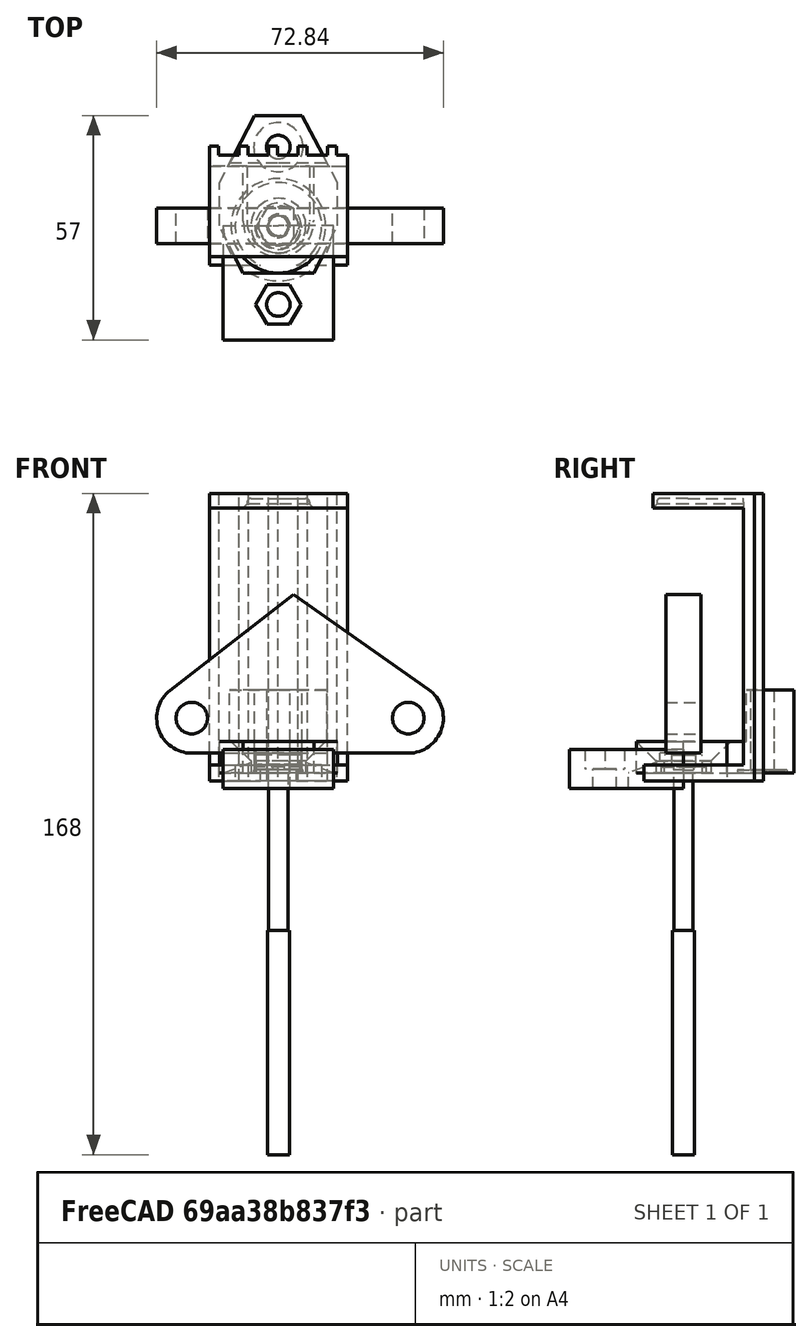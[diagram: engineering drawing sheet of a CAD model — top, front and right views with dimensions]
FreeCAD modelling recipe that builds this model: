
FCSTD DOCUMENT  (FreeCAD 1.0R1.0.1)
Label: stopper
License: All rights reserved
LicenseURL: http://en.wikipedia.org/wiki/All_rights_reserved
objects: Sketcher::SketchObject×19, PartDesign::Pad×12, App::Link×8, App::FeaturePython×8, PartDesign::Body×6, PartDesign::Pocket×4, PartDesign::Chamfer×3, Assembly::JointGroup×2, Assembly::AssemblyObject×2, Part::Revolution×1, Part::Extrusion×1, Image::ImagePlane×1, PartDesign::LinearPattern×1, PartDesign::Fillet×1, PartDesign::FeatureBase×1, Assembly::AssemblyLink×1, PartDesign::Revolution×1
note: 113 computed .brp shape members not serialized (recipe doc carries the construction recipe); baked Part::Feature solids carry a one-line shape summary decoded from their .brp

FEATURE [Sketcher::SketchObject] Sketch  label="Cyl"
  ArcFitTolerance = 1e-06
  FullyConstrained = true
  MakeInternals = false
  Placement = pos=(0,0,0) rot=(1,0,0;1.5708rad)
  sketch-geometry (15):
    g0: LineSegment StartX=0 StartY=0 StartZ=0 EndX=8 EndY=0 EndZ=0
    g1: LineSegment StartX=8 StartY=0 StartZ=0 EndX=14 EndY=6 EndZ=0
    g2: LineSegment StartX=14 StartY=6 StartZ=0 EndX=14 EndY=36.824 EndZ=0
    g3: LineSegment StartX=14 StartY=36.824 StartZ=0 EndX=15.2 EndY=36.824 EndZ=0
    g4: LineSegment StartX=15.2 StartY=36.824 StartZ=0 EndX=14.8 EndY=37.9406 EndZ=0
    g5: LineSegment StartX=14.8 StartY=37.9406 StartZ=0 EndX=14.8 EndY=53 EndZ=0
    g6: LineSegment StartX=14.8 StartY=53 StartZ=0 EndX=12.5 EndY=56 EndZ=0
    g7: LineSegment StartX=12.5 StartY=56 StartZ=0 EndX=12.5 EndY=62.6 EndZ=0
    g8: LineSegment StartX=12.5 StartY=62.6 StartZ=0 EndX=6 EndY=65.6 EndZ=0
    g9: LineSegment StartX=6 StartY=65.6 StartZ=0 EndX=6 EndY=67.6 EndZ=0
    g10: LineSegment StartX=6 StartY=67.6 StartZ=0 EndX=0 EndY=67.6 EndZ=0
    g11: LineSegment StartX=0 StartY=-0.8 StartZ=0 EndX=6.56 EndY=-0.8 EndZ=0
    g12: LineSegment StartX=6.56 StartY=-0.8 StartZ=0 EndX=6.56 EndY=0 EndZ=0
    g13: LineSegment StartX=0 StartY=-4.1 StartZ=0 EndX=4 EndY=-4.1 EndZ=0
    g14: LineSegment StartX=4 StartY=-4.1 StartZ=0 EndX=4 EndY=-0.8 EndZ=0
  constraints (46):
    c: Coincident(g-1,g0)
    c: PointOnObject(g0,g-1)
    c: Coincident(g0,g1)
    c: Coincident(g1,g2)
    c: Vertical(g2)
    c: Coincident(g2,g3)
    c: Coincident(g3,g4)
    c: Coincident(g4,g5)
    c: Vertical(g5)
    c: Coincident(g5,g6)
    c: Angle(g1,g-1) = 2.35619
    c: DistanceX(g0,g0) = 8
    c: Distance(g2,g-2) = 14
    c: Distance(g3,g-2) = 15.2
    c: Horizontal(g3)
    c: Distance(g5,g-2) = 14.8
    c: Block(g4)
    c: Distance(g6,g-1) = 56
    c: Coincident(g6,g7)
    c: Vertical(g7)
    c: Coincident(g7,g8)
    c: DistanceY(g7,g7) = 6.6
    c: Distance(g7,g-2) = 12.5
    c: DistanceY(g6,g6) = 3
    c: DistanceY(g7,g8) = 3
    c: Distance(g8,g-2) = 6
    c: Coincident(g8,g9)
    c: Vertical(g9)
    c: Coincident(g9,g10)
    c: PointOnObject(g10,g-2)
    c: Horizontal(g10)
    c: DistanceY(g9,g9) = 2
    c: PointOnObject(g11,g-2)
    c: Horizontal(g11)
    c: Coincident(g11,g12)
    c: PointOnObject(g12,g0)
    c: Vertical(g12)
    c: DistanceX(g11,g11) = 6.56
    c: DistanceY(g12,g12) = 0.8
    c: PointOnObject(g13,g-2)
    c: Horizontal(g13)
    c: Coincident(g13,g14)
    c: PointOnObject(g14,g11)
    c: Vertical(g14)
    c: DistanceX(g13,g13) = 4
    c: DistanceY(g14,g14) = 3.3
FEATURE [Sketcher::SketchObject] Sketch001  label="boss-s"
  ArcFitTolerance = 1e-06
  FullyConstrained = false
  MakeInternals = false
  Placement = pos=(0,0,0) rot=(1,0,0;1.5708rad)
  sketch-geometry (8):
    g0: LineSegment StartX=0 StartY=5 StartZ=0 EndX=33 EndY=5 EndZ=0
    g1: ArcOfCircle CenterX=33 CenterY=13.9161 CenterZ=0 NormalX=0 NormalY=0 NormalZ=1 AngleXU=0 Radius=8.91608 StartAngle=4.71239 EndAngle=7.24
    g2: LineSegment StartX=38.1368 StartY=21.2037 StartZ=0 EndX=3.88315 EndY=45.3479 EndZ=0
    g3: LineSegment StartX=3.88315 StartY=45.3479 StartZ=0 EndX=-27.4747 EndY=20.9535 EndZ=0
    g4: ArcOfCircle CenterX=-22 CenterY=13.9161 CenterZ=0 NormalX=0 NormalY=0 NormalZ=1 AngleXU=0 Radius=8.91608 StartAngle=2.23194 EndAngle=4.71239
    g5: LineSegment StartX=-22 StartY=5 StartZ=0 EndX=0 EndY=5 EndZ=0
    g6: Circle CenterX=-22 CenterY=13.9161 CenterZ=0 NormalX=0 NormalY=0 NormalZ=1 AngleXU=0 Radius=4
    g7: Circle CenterX=33 CenterY=13.9161 CenterZ=0 NormalX=0 NormalY=0 NormalZ=1 AngleXU=0 Radius=4
  constraints (17):
    c: PointOnObject(g0,g-2)
    c: Horizontal(g0)
    c: Tangent(g0,g1) = -1.5708
    c: Tangent(g1,g2) = -1.5708
    c: Coincident(g2,g3)
    c: Tangent(g3,g4) = -1.5708
    c: Tangent(g4,g5) = -1.5708
    c: Coincident(g5,g0)
    c: Horizontal(g4,g1)
    c: Distance(g1,g-2) = 33
    c: Distance(g4,g-2) = 22
    c: Parallel(g5,g0)
    c: Distance(g-1,g0) = 5
    c: Coincident(g6,g4)
    c: Diameter(g6) = 8
    c: Coincident(g7,g1)
    c: Diameter(g7) = 8
FEATURE [Part::Revolution] Revolve  label="cylinterd"
  Angle = 360
  Axis = (0,0,1)
  Base = (0,0,0)
  FaceMakerClass = Part::FaceMakerBullseye
  Solid = false
  Source = -> Sketch
  Symmetric = false
FEATURE [Part::Extrusion] Extrude  label="boss"
  Base = -> Sketch001
  Dir = (0,-1,2e-16)
  DirMode = 2
  FaceMakerClass = Part::FaceMakerBullseye
  FaceMakerMode = 3
  LengthFwd = 9
  LengthRev = 0
  Solid = true
  Symmetric = true
FEATURE [Image::ImagePlane] oemtension
  Placement = pos=(5.44,31.83,30.09) rot=(0.839369,-0.207279,0.502488;2.2068rad)
  XSize = 98.798
  YSize = 74.102
FEATURE [Sketcher::SketchObject] Sketch004  label="retainR-s"
  ArcFitTolerance = 1e-06
  AttachmentSupport = -> [XY_Plane]
  FullyConstrained = true
  MakeInternals = false
  MapMode = 5
  sketch-geometry (7):
    g0: LineSegment StartX=17.5 StartY=-10 StartZ=0 EndX=17.5 EndY=18 EndZ=0
    g1: LineSegment StartX=17.5 StartY=18 StartZ=0 EndX=-17.5 EndY=18 EndZ=0
    g2: LineSegment StartX=-17.5 StartY=18 StartZ=0 EndX=-17.5 EndY=-10 EndZ=0
    g3: LineSegment StartX=-17.5 StartY=-10 StartZ=0 EndX=-4.58258 EndY=-10 EndZ=0
    g4: GeomPoint X=0 Y=18 Z=0
    g5: ArcOfCircle CenterX=0 CenterY=0 CenterZ=0 NormalX=0 NormalY=0 NormalZ=1 AngleXU=0 Radius=11 StartAngle=5.14209 EndAngle=10.5659
    g6: LineSegment StartX=4.58258 StartY=-10 StartZ=0 EndX=17.5 EndY=-10 EndZ=0
  constraints (20):
    c: Coincident(g0,g1)
    c: Coincident(g1,g2)
    c: Coincident(g2,g3)
    c: Coincident(g6,g0)
    c: Vertical(g0)
    c: Vertical(g2)
    c: Horizontal(g1)
    c: Horizontal(g3)
    c: Distance(g1,g1) = 35
    c: DistanceY(g0,g0) = 28
    c: PointOnObject(g4,g-2)
    c: Distance(g1,g-1) = 18
    c: Symmetric(g1,g0,g4)
    c: Coincident(g5,g-1)
    c: Diameter(g5) = 22
    c: PointOnObject(g5,g6)
    c: Coincident(g3,g5)
    c: PointOnObject(g6,g5)
    c: Horizontal(g6)
    c: Distance(g1,g3) = 28
FEATURE [PartDesign::Pad] Pad  label="ring"
  Direction = (0,0,1)
  Length = 4
  Length2 = 10
  Midplane = true
  Profile = -> Sketch004
  ReferenceAxis = -> Sketch004 [N_Axis]
  Suppressed = false
  Type = 0
FEATURE [Sketcher::SketchObject] Sketch005  label="reatinback-s"
  ArcFitTolerance = 1e-06
  AttachmentSupport = -> [Pad]
  ExternalGeometry = -> [Pad]
  FullyConstrained = true
  MakeInternals = false
  MapMode = 5
  Placement = pos=(0,0,2) rot=(0,0,1;0rad)
  sketch-geometry (4):
    g0: LineSegment StartX=17.5 StartY=18 StartZ=0 EndX=-17.5 EndY=18 EndZ=0
    g1: LineSegment StartX=-17.5 StartY=18 StartZ=0 EndX=-17.5 EndY=15.2 EndZ=0
    g2: LineSegment StartX=-17.5 StartY=15.2 StartZ=0 EndX=17.5 EndY=15.2 EndZ=0
    g3: LineSegment StartX=17.5 StartY=15.2 StartZ=0 EndX=17.5 EndY=18 EndZ=0
  constraints (10):
    c: Coincident(g0,g1)
    c: Coincident(g1,g2)
    c: Coincident(g2,g3)
    c: Coincident(g3,g0)
    c: Horizontal(g2)
    c: Vertical(g1)
    c: Vertical(g3)
    c: Coincident(g-3,g0)
    c: Coincident(g0,g-3)
    c: DistanceY(g3,g3) = 2.8
FEATURE [PartDesign::Pad] Pad001  label="spine"
  BaseFeature = -> Pad
  Direction = (0,0,1)
  Length = 69
  Length2 = 10
  Profile = -> Sketch005
  ReferenceAxis = -> Sketch005 [N_Axis]
  Suppressed = false
  Type = 0
FEATURE [Sketcher::SketchObject] Sketch006
  ArcFitTolerance = 1e-06
  AttachmentSupport = -> [Pad001]
  ExternalGeometry = -> [Pad001]
  FullyConstrained = true
  MakeInternals = false
  MapMode = 5
  Placement = pos=(0,15.2,0) rot=(1,0,0;1.5708rad)
  sketch-geometry (5):
    g0: LineSegment StartX=-17.5 StartY=71 StartZ=0 EndX=-17.5 EndY=69.75 EndZ=0
    g1: LineSegment StartX=-17.5 StartY=69.75 StartZ=0 EndX=17.5 EndY=69.75 EndZ=0
    g2: LineSegment StartX=17.5 StartY=69.75 StartZ=0 EndX=17.5 EndY=71 EndZ=0
    g3: LineSegment StartX=17.5 StartY=71 StartZ=0 EndX=-17.5 EndY=71 EndZ=0
    g4: GeomPoint X=3.6e-15 Y=71 Z=0
  constraints (11):
    c: Coincident(g0,g1)
    c: Coincident(g1,g2)
    c: Coincident(g2,g3)
    c: Coincident(g3,g0)
    c: Vertical(g0)
    c: Vertical(g2)
    c: Horizontal(g1)
    c: Symmetric(g-3,g-3,g4)
    c: Coincident(g2,g-3)
    c: Coincident(g0,g-3)
    c: DistanceY(g0,g0) = 1.25
FEATURE [PartDesign::Pad] Pad002  label="fngr"
  BaseFeature = -> Pad001
  Direction = (0,-1,2e-16)
  Length = 23
  Length2 = 10
  Profile = -> Sketch006
  ReferenceAxis = -> Sketch006 [N_Axis]
  Suppressed = false
  Type = 0
FEATURE [Sketcher::SketchObject] Sketch007
  ArcFitTolerance = 1e-06
  AttachmentSupport = -> [Pad001]
  ExternalGeometry = -> [Pad001]
  FullyConstrained = true
  MakeInternals = false
  MapMode = 5
  Placement = pos=(0,18,0) rot=(0,0.707107,0.707107;3.14159rad)
  sketch-geometry (5):
    g0: LineSegment StartX=17.5 StartY=-2 StartZ=0 EndX=17.5 EndY=71 EndZ=0
    g1: LineSegment StartX=17.5 StartY=71 StartZ=0 EndX=15.2 EndY=71 EndZ=0
    g2: LineSegment StartX=15.2 StartY=71 StartZ=0 EndX=15.2 EndY=-2 EndZ=0
    g3: LineSegment StartX=15.2 StartY=-2 StartZ=0 EndX=17.5 EndY=-2 EndZ=0
    g4: GeomPoint X=16.35 Y=34.5 Z=0
  constraints (10):
    c: Coincident(g0,g1)
    c: Coincident(g1,g2)
    c: Coincident(g2,g3)
    c: Coincident(g3,g0)
    c: Horizontal(g1)
    c: Symmetric(g1,g0,g4)
    c: Symmetric(g2,g0,g4)
    c: DistanceX(g3,g3) = 2.3
    c: Coincident(g0,g-4)
    c: Coincident(g0,g-5)
FEATURE [PartDesign::Pad] Pad003  label="rib"
  BaseFeature = -> Pad002
  Direction = (0,1,-2e-16)
  Length = 2.3
  Length2 = 10
  Profile = -> Sketch007
  ReferenceAxis = -> Sketch007 [N_Axis]
  Suppressed = false
  Type = 0
FEATURE [PartDesign::LinearPattern] LinearPattern
  BaseFeature = -> Pad003
  Direction = -> Sketch007 [H_Axis]
  Length = 30
  Mode = 0
  Occurrences = 5
  Offset = 7.5
  Originals = -> [Pad003]
  Reversed = true
  Suppressed = false
  TransformMode = 0
FEATURE [Sketcher::SketchObject] Sketch008
  ArcFitTolerance = 1e-06
  AttachmentSupport = -> [LinearPattern]
  ExternalGeometry = -> [LinearPattern]
  FullyConstrained = true
  MakeInternals = false
  MapMode = 5
  Placement = pos=(0,1.53e-14,69.75) rot=(1,0,0;3.14159rad)
  sketch-geometry (12):
    g0: LineSegment StartX=-17.5 StartY=-15.2 StartZ=0 EndX=-17.5 EndY=7.8 EndZ=0
    g1: LineSegment StartX=-17.5 StartY=7.8 StartZ=0 EndX=0 EndY=7.8 EndZ=0
    g2: LineSegment StartX=7e-16 StartY=7.8 StartZ=0 EndX=7e-16 EndY=6.8 EndZ=0
    g3: ArcOfCircle CenterX=-1.6e-15 CenterY=-1.14 CenterZ=0 NormalX=0 NormalY=0 NormalZ=1 AngleXU=0 Radius=7.94 StartAngle=1.5708 EndAngle=3.14159
    g4: LineSegment StartX=-7.94 StartY=-1.14 StartZ=0 EndX=-7.94 EndY=-15.2 EndZ=0
    g5: LineSegment StartX=-7.94 StartY=-15.2 StartZ=0 EndX=-17.5 EndY=-15.2 EndZ=0
    g6: LineSegment StartX=17.5 StartY=-15.2 StartZ=0 EndX=17.5 EndY=7.8 EndZ=0
    g7: LineSegment StartX=17.5 StartY=7.8 StartZ=0 EndX=7.1e-15 EndY=7.8 EndZ=0
    g8: LineSegment StartX=7.1e-15 StartY=7.8 StartZ=0 EndX=7.1e-15 EndY=6.8 EndZ=0
    g9: ArcOfCircle CenterX=3.7e-15 CenterY=-1.14 CenterZ=0 NormalX=0 NormalY=0 NormalZ=1 AngleXU=0 Radius=7.94 StartAngle=1e-16 EndAngle=1.5708
    g10: LineSegment StartX=7.94 StartY=-1.14 StartZ=0 EndX=7.94 EndY=-15.2 EndZ=0
    g11: LineSegment StartX=7.94 StartY=-15.2 StartZ=0 EndX=17.5 EndY=-15.2 EndZ=0
  constraints (31):
    c: Coincident(g0,g1)
    c: PointOnObject(g1,g-2)
    c: Horizontal(g1)
    c: Coincident(g1,g2)
    c: Vertical(g2)
    c: Perpendicular(g2,g3) = 4.71239
    c: Tangent(g3,g4) = -1.5708
    c: Coincident(g4,g5)
    c: Coincident(g5,g0)
    c: Horizontal(g5)
    c: Coincident(g0,g-4)
    c: Coincident(g0,g-5)
    c: DistanceY(g2,g2) = 1
    c: Radius(g3) = 7.94
    c: Vertical(g4)
    c: Coincident(g6,g7)
    c: Horizontal(g7)
    c: Coincident(g7,g8)
    c: Vertical(g8)
    c: Perpendicular(g8,g9) = 4.71239
    c: Tangent(g9,g10) = 1.5708
    c: Coincident(g10,g11)
    c: Coincident(g11,g6)
    c: Horizontal(g11)
    c: Radius(g9) = 7.94
    c: Vertical(g10)
    c: Equal(g6,g0)
    c: Equal(g11,g5)
    c: Equal(g7,g1)
    c: Equal(g10,g4)
    c: Coincident(g-6,g6)
FEATURE [PartDesign::Pad] Pad004  label="pret"
  BaseFeature = -> LinearPattern
  Direction = (0,0,-1)
  Length = 2.4
  Length2 = 10
  Profile = -> Sketch008
  ReferenceAxis = -> Sketch008 [N_Axis]
  Suppressed = false
  Type = 0
FEATURE [PartDesign::Fillet] Fillet
  Base = -> Pad004 [Edge129]
  BaseFeature = -> Pad004
  Radius = 1
  SupportTransform = false
  Suppressed = false
  UseAllEdges = false
FEATURE [PartDesign::Chamfer] Chamfer
  Angle = 45
  Base = -> Fillet [Edge36]
  BaseFeature = -> Fillet
  ChamferType = 0
  FlipDirection = false
  Size = 1
  Size2 = 1
  SupportTransform = false
  Suppressed = false
  UseAllEdges = false
FEATURE [PartDesign::Body] Body  label="xxstopper"
  AllowCompound = false
  Group = -> [Sketch004,Pad,Sketch005,Pad001,Sketch006,Pad002,Sketch007,Pad003,LinearPattern,Sketch008,Pad004,Fillet,Chamfer]
  Origin = -> Origin
  Tip = -> Chamfer
FEATURE [Sketcher::SketchObject] Sketch009  label="hd"
  ArcFitTolerance = 1e-06
  AttachmentSupport = -> [XY_Plane001]
  FullyConstrained = true
  MakeInternals = false
  MapMode = 5
  sketch-geometry (1):
    g0: Circle CenterX=0 CenterY=0 CenterZ=0 NormalX=0 NormalY=0 NormalZ=1 AngleXU=0 Radius=5.75
  constraints (2):
    c: Coincident(g0,g-1)
    c: Diameter(g0) = 11.5
FEATURE [PartDesign::Pad] Pad005
  Direction = (0,0,1)
  Length = 2.2
  Length2 = 10
  Profile = -> Sketch009 [Edge1]
  ReferenceAxis = -> Sketch009 [N_Axis]
  Suppressed = false
  Type = 0
FEATURE [Sketcher::SketchObject] Sketch010
  ArcFitTolerance = 1e-06
  AttachmentSupport = -> [Pad005]
  FullyConstrained = true
  MakeInternals = false
  MapMode = 5
  Placement = pos=(0,0,2.2) rot=(0,0,1;0rad)
  sketch-geometry (7):
    g0: LineSegment StartX=2.88675 StartY=0 StartZ=0 EndX=1.44338 EndY=2.5 EndZ=0
    g1: LineSegment StartX=1.44338 StartY=2.5 StartZ=0 EndX=-1.44338 EndY=2.5 EndZ=0
    g2: LineSegment StartX=-1.44338 StartY=2.5 StartZ=0 EndX=-2.88675 EndY=7.034e-13 EndZ=0
    g3: LineSegment StartX=-2.88675 StartY=7.034e-13 StartZ=0 EndX=-1.44338 EndY=-2.5 EndZ=0
    g4: LineSegment StartX=-1.44338 StartY=-2.5 StartZ=0 EndX=1.44338 EndY=-2.5 EndZ=0
    g5: LineSegment StartX=1.44338 StartY=-2.5 StartZ=0 EndX=2.88675 EndY=0 EndZ=0
    g6: Circle [constr] CenterX=0 CenterY=0 CenterZ=0 NormalX=0 NormalY=0 NormalZ=1 AngleXU=0 Radius=2.88675
  constraints (16):
    c: Coincident(g0,g1)
    c: Coincident(g1,g2)
    c: Coincident(g2,g3)
    c: Coincident(g3,g4)
    c: Coincident(g4,g5)
    c: Coincident(g5,g0)
    c: Equal(g0, g1-g5) x5
    c: PointOnObject(g0,g6)
    c: PointOnObject(g1,g6)
    c: PointOnObject(g2,g6)
    c: PointOnObject(g3,g6)
    c: PointOnObject(g4,g6)
    c: PointOnObject(g5,g6)
    c: Coincident(g6,g-1)
    c: PointOnObject(g5,g-1)
    c: DistanceY(g4,g0) = 5
FEATURE [PartDesign::Pocket] Pocket
  BaseFeature = -> Pad005
  Direction = (0,0,-1)
  Length = 1.4
  Length2 = 5
  Profile = -> Sketch010
  ReferenceAxis = -> Sketch010 [N_Axis]
  Suppressed = false
  Type = 0
FEATURE [PartDesign::Chamfer] Chamfer001
  Angle = 45
  Base = -> Pocket [Edge3]
  BaseFeature = -> Pocket
  ChamferType = 0
  FlipDirection = false
  Size = 0.7
  Size2 = 1
  SupportTransform = false
  Suppressed = false
  UseAllEdges = false
FEATURE [Sketcher::SketchObject] Sketch011
  ArcFitTolerance = 1e-06
  AttachmentSupport = -> [Chamfer001]
  FullyConstrained = true
  MakeInternals = false
  MapMode = 5
  Placement = pos=(0,0,0) rot=(1,0,0;3.14159rad)
  sketch-geometry (1):
    g0: Circle CenterX=0 CenterY=0 CenterZ=0 NormalX=0 NormalY=0 NormalZ=1 AngleXU=0 Radius=2.45
  constraints (2):
    c: Coincident(g0,g-1)
    c: Diameter(g0) = 4.9
FEATURE [PartDesign::Pad] Pad006
  BaseFeature = -> Chamfer001
  Direction = (0,0,-1)
  Length = 40
  Length2 = 10
  Profile = -> Sketch011
  ReferenceAxis = -> Sketch011 [N_Axis]
  Suppressed = false
  Type = 0
FEATURE [Sketcher::SketchObject] Sketch012
  ArcFitTolerance = 1e-06
  AttachmentSupport = -> [Pad006]
  FullyConstrained = true
  MakeInternals = false
  MapMode = 5
  Placement = pos=(0,0,-40) rot=(1,0,0;3.14159rad)
  sketch-geometry (1):
    g0: Circle CenterX=0 CenterY=0 CenterZ=0 NormalX=0 NormalY=0 NormalZ=1 AngleXU=0 Radius=2.8
  constraints (2):
    c: Coincident(g0,g-1)
    c: Diameter(g0) = 5.6
FEATURE [PartDesign::Pad] Pad007
  BaseFeature = -> Pad006
  Direction = (0,0,-1)
  Length = 57
  Length2 = 10
  Profile = -> Sketch012
  ReferenceAxis = -> Sketch012 [N_Axis]
  Suppressed = false
  Type = 0
FEATURE [PartDesign::Body] Body001  label="m6"
  AllowCompound = false
  Group = -> [Sketch009,Pad005,Sketch010,Pocket,Chamfer001,Sketch011,Pad006,Sketch012,Pad007]
  Origin = -> Origin001
  Tip = -> Pad007
FEATURE [Sketcher::SketchObject] Sketch013
  ArcFitTolerance = 1e-06
  AttachmentSupport = -> [XY_Plane002]
  FullyConstrained = true
  MakeInternals = false
  MapMode = 5
  sketch-geometry (8):
    g0: LineSegment StartX=5.54256 StartY=0 StartZ=0 EndX=2.77128 EndY=4.8 EndZ=0
    g1: LineSegment StartX=2.77128 StartY=4.8 StartZ=0 EndX=-2.77128 EndY=4.8 EndZ=0
    g2: LineSegment StartX=-2.77128 StartY=4.8 StartZ=0 EndX=-5.54256 EndY=-9e-16 EndZ=0
    g3: LineSegment StartX=-5.54256 StartY=-9e-16 StartZ=0 EndX=-2.77128 EndY=-4.8 EndZ=0
    g4: LineSegment StartX=-2.77128 StartY=-4.8 StartZ=0 EndX=2.77128 EndY=-4.8 EndZ=0
    g5: LineSegment StartX=2.77128 StartY=-4.8 StartZ=0 EndX=5.54256 EndY=0 EndZ=0
    g6: Circle [constr] CenterX=0 CenterY=0 CenterZ=0 NormalX=0 NormalY=0 NormalZ=1 AngleXU=0 Radius=5.54256
    g7: Circle CenterX=0 CenterY=0 CenterZ=0 NormalX=0 NormalY=0 NormalZ=1 AngleXU=0 Radius=3
  constraints (18):
    c: Coincident(g0,g1)
    c: Coincident(g1,g2)
    c: Coincident(g2,g3)
    c: Coincident(g3,g4)
    c: Coincident(g4,g5)
    c: Coincident(g5,g0)
    c: Equal(g0, g1-g5) x5
    c: PointOnObject(g0,g6)
    c: PointOnObject(g1,g6)
    c: PointOnObject(g2,g6)
    c: PointOnObject(g3,g6)
    c: PointOnObject(g4,g6)
    c: PointOnObject(g5,g6)
    c: Coincident(g6,g-1)
    c: PointOnObject(g5,g-1)
    c: DistanceY(g4,g0) = 9.6  'tenish'
    c: Coincident(g7,g6)
    c: Diameter(g7) = 6
FEATURE [PartDesign::Pad] Pad008
  Direction = (0,0,1)
  Length = 4.6
  Length2 = 10
  Profile = -> Sketch013
  ReferenceAxis = -> Sketch013 [N_Axis]
  Suppressed = false
  Type = 0
FEATURE [PartDesign::Body] Body002  label="m6b"
  AllowCompound = false
  Group = -> [Sketch013,Pad008]
  Origin = -> Origin002
  Tip = -> Pad008
FEATURE [App::Link] m6  label="bolt"
  LinkedObject = -> Body001
FEATURE [App::FeaturePython] GroundedJoint  # Assembly grounded joint (typed FeaturePython)
  ObjectToGround = -> m6
FEATURE [App::Link] m6b  label="nut"
  LinkPlacement = pos=(-0.115494,0.200204,-68) rot=(0.999998,7e-06,-0.002062;3.14874rad)
  LinkedObject = -> Body002
  Placement = pos=(-0.115494,0.200204,-68) rot=(0.999998,7e-06,-0.002062;3.14874rad)
FEATURE [App::FeaturePython] Joint  label="Cylindrical"  # Assembly joint (typed FeaturePython)
  Activated = true
  AngleMax = 0
  AngleMin = 0
  Detach1 = false
  Detach2 = false
  Distance = 0
  Distance2 = 0
  EnableAngleMax = false
  EnableAngleMin = false
  EnableLengthMax = false
  EnableLengthMin = false
  JointType = 2 (Cylindrical)
  LengthMax = 0
  LengthMin = 0
  Placement1 = pos=(0,1e-16,2.3) rot=(0,0,1;0rad)
  Placement2 = pos=(0,0,-40) rot=(1,0,0;3.14159rad)
  Reference1 = -> Assembly [m6b.Face7,m6b.Face7]
  Reference2 = -> Assembly [m6.Face14,m6.Edge2]
FEATURE [App::FeaturePython] Joint001  label="Distance"  # Assembly joint (typed FeaturePython)
  Activated = true
  AngleMax = 0
  AngleMin = 0
  Detach1 = false
  Detach2 = false
  Distance = -68
  Distance2 = 0
  EnableAngleMax = false
  EnableAngleMin = false
  EnableLengthMax = false
  EnableLengthMin = false
  JointType = 5 (Distance)
  LengthMax = 0
  LengthMin = 0
  Placement1 = pos=(0,-4e-16,0) rot=(0,0,1;0rad)
  Placement2 = pos=(-1e-16,-3e-16,0) rot=(0,0,1;0rad)
  Reference1 = -> Assembly [m6.Face3,m6.Face3]
  Reference2 = -> Assembly [m6b.Face8,m6b.Vertex1]
FEATURE [Sketcher::SketchObject] Sketch014
  ArcFitTolerance = 1e-06
  AttachmentSupport = -> [XY_Plane004]
  FullyConstrained = true
  MakeInternals = false
  MapMode = 5
  sketch-geometry (12):
    g0: Circle CenterX=0 CenterY=0 CenterZ=0 NormalX=0 NormalY=0 NormalZ=1 AngleXU=0 Radius=7
    g1: Circle CenterX=0 CenterY=20 CenterZ=0 NormalX=0 NormalY=0 NormalZ=1 AngleXU=0 Radius=3
    g2: LineSegment StartX=0 StartY=-12 StartZ=0 EndX=9 EndY=-12 EndZ=0
    g3: LineSegment StartX=9 StartY=-12 StartZ=0 EndX=15 EndY=0 EndZ=0
    g4: LineSegment StartX=15 StartY=0 StartZ=0 EndX=15 EndY=11 EndZ=0
    g5: LineSegment StartX=15 StartY=11 StartZ=0 EndX=6 EndY=28 EndZ=0
    g6: LineSegment StartX=6 StartY=28 StartZ=0 EndX=0 EndY=28 EndZ=0
    g7: LineSegment StartX=-6 StartY=28 StartZ=0 EndX=0 EndY=28 EndZ=0
    g8: LineSegment StartX=-15 StartY=11 StartZ=0 EndX=-6 EndY=28 EndZ=0
    g9: LineSegment StartX=-15 StartY=0 StartZ=0 EndX=-15 EndY=11 EndZ=0
    g10: LineSegment StartX=-9 StartY=-12 StartZ=0 EndX=-15 EndY=0 EndZ=0
    g11: LineSegment StartX=-9 StartY=-12 StartZ=0 EndX=0 EndY=-12 EndZ=0
  constraints (31):
    c: Coincident(g0,g-1)
    c: Diameter(g0) = 14
    c: PointOnObject(g1,g-2)
    c: DistanceY(g0,g1) = 20
    c: Diameter(g1) = 6
    c: PointOnObject(g2,g-2)
    c: Horizontal(g2)
    c: Coincident(g2,g3)
    c: Coincident(g3,g4)
    c: Coincident(g4,g5)
    c: Coincident(g5,g6)
    c: PointOnObject(g6,g-2)
    c: Horizontal(g6)
    c: DistanceX(g6,g6) = 6
    c: DistanceY(g1,g6) = 8
    c: DistanceX(g-1,g4) = 15
    c: Vertical(g4)
    c: DistanceY(g2,g0) = 12
    c: PointOnObject(g3,g-1)
    c: DistanceX(g2,g2) = 9
    c: DistanceY(g3,g4) = 11
    c: Symmetric(g3,g10,g-2)
    c: Symmetric(g3,g10,g-2)
    c: Symmetric(g4,g9,g-2)
    c: Symmetric(g4,g9,g-2)
    c: Symmetric(g5,g8,g-2)
    c: Symmetric(g5,g8,g-2)
    c: Symmetric(g6,g7,g-2)
    c: Coincident(g11,g10)
    c: Coincident(g11,g2)
    c: Coincident(g7,g6)
FEATURE [PartDesign::Pad] Pad009
  Direction = (0,0,1)
  Length = 8
  Length2 = 10
  Profile = -> Sketch014
  ReferenceAxis = -> Sketch014 [N_Axis]
  Suppressed = false
  Type = 0
FEATURE [Sketcher::SketchObject] Sketch015
  ArcFitTolerance = 1e-06
  AttachmentSupport = -> [Pad009]
  ExternalGeometry = -> [Pad009]
  FullyConstrained = true
  MakeInternals = false
  MapMode = 5
  Placement = pos=(0,0,0) rot=(1,0,0;3.14159rad)
  sketch-geometry (1):
    g0: Circle CenterX=0 CenterY=-20 CenterZ=0 NormalX=0 NormalY=0 NormalZ=1 AngleXU=0 Radius=6.25
  constraints (2):
    c: Coincident(g0,g-3)
    c: Diameter(g0) = 12.5
FEATURE [PartDesign::Pocket] Pocket001
  BaseFeature = -> Pad009
  Direction = (0,0,1)
  Length = 0.8
  Length2 = 5
  Profile = -> Sketch015
  ReferenceAxis = -> Sketch015 [N_Axis]
  Suppressed = false
  Type = 0
FEATURE [PartDesign::Chamfer] Chamfer002
  Angle = 45
  Base = -> Pocket001 [Edge27]
  BaseFeature = -> Pocket001
  ChamferType = 2
  FlipDirection = false
  Size = 5
  Size2 = 1
  SupportTransform = false
  Suppressed = false
  UseAllEdges = false
FEATURE [Sketcher::SketchObject] Sketch016
  ArcFitTolerance = 1e-06
  AttachmentSupport = -> [Chamfer002]
  ExternalGeometry = -> [Chamfer002]
  FullyConstrained = true
  MakeInternals = false
  MapMode = 5
  Placement = pos=(0,0,8) rot=(0,0,1;0rad)
  sketch-geometry (6):
    g0: Circle CenterX=0 CenterY=20 CenterZ=0 NormalX=0 NormalY=0 NormalZ=1 AngleXU=0 Radius=3
    g1: LineSegment StartX=0 StartY=16 StartZ=0 EndX=12.3529 EndY=16 EndZ=0
    g2: LineSegment StartX=12.3529 StartY=16 StartZ=0 EndX=6 EndY=28 EndZ=0
    g3: LineSegment StartX=6 StartY=28 StartZ=0 EndX=-6 EndY=28 EndZ=0
    g4: LineSegment StartX=-6 StartY=28 StartZ=0 EndX=-12.3529 EndY=16 EndZ=0
    g5: LineSegment StartX=-12.3529 StartY=16 StartZ=0 EndX=0 EndY=16 EndZ=0
  constraints (15):
    c: Equal(g-3,g0)
    c: PointOnObject(g1,g-2)
    c: PointOnObject(g1,g-6)
    c: Horizontal(g1)
    c: Coincident(g1,g2)
    c: Coincident(g2,g-6)
    c: Coincident(g2,g3)
    c: Coincident(g3,g-7)
    c: Coincident(g3,g4)
    c: PointOnObject(g4,g-7)
    c: Coincident(g4,g5)
    c: Coincident(g5,g1)
    c: Horizontal(g5)
    c: DistanceY(g1,g0) = 4
    c: Coincident(g0,g-3)
FEATURE [App::Link] tailhk  label="tailhk001"
  LinkPlacement = pos=(0,20,0.8) rot=(1,0,0;3.14159rad)
  LinkedObject = -> Body003
  Placement = pos=(0,20,0.8) rot=(1,0,0;3.14159rad)
FEATURE [App::FeaturePython] Joint002  label="Cylindrical001"  # Assembly joint (typed FeaturePython)
  Activated = true
  AngleMax = 0
  AngleMin = 0
  Detach1 = false
  Detach2 = false
  Distance = 0
  Distance2 = 0
  EnableAngleMax = false
  EnableAngleMin = false
  EnableLengthMax = false
  EnableLengthMin = false
  JointType = 2 (Cylindrical)
  LengthMax = 0
  LengthMin = 0
  Placement1 = pos=(0,0,0) rot=(1,0,0;3.14159rad)
  Placement2 = pos=(0,20,0.8) rot=(-1,0,0;3.14159rad)
  Reference1 = -> Assembly [m6.Face5,m6.Edge2]
  Reference2 = -> Assembly [tailhk.?Face22,tailhk.Edge3]
FEATURE [App::FeaturePython] Joint003  label="Fixed"  # Assembly joint (typed FeaturePython)
  Activated = true
  AngleMax = 0
  AngleMin = 0
  Detach1 = false
  Detach2 = false
  Distance = 0
  Distance2 = 0
  EnableAngleMax = false
  EnableAngleMin = false
  EnableLengthMax = false
  EnableLengthMin = false
  JointType = 0 (Fixed)
  LengthMax = 0
  LengthMin = 0
  Placement1 = pos=(0,-4e-16,0) rot=(0,0,1;0rad)
  Placement2 = pos=(0,20,0.8) rot=(0,0,1;0rad)
  Reference1 = -> Assembly [m6.Face3,m6.Face3]
  Reference2 = -> Assembly [tailhk.Face23,tailhk.Face23]
FEATURE [PartDesign::FeatureBase] BaseFeature
  BaseFeature = -> Extrude
  Suppressed = false
FEATURE [PartDesign::Body] Body004  label="Body"
  AllowCompound = false
  BaseFeature = -> Extrude
  Group = -> [BaseFeature]
  Origin = -> Origin005
  Tip = -> BaseFeature
FEATURE [App::Link] cylinterd  label="cylinterd001"
  LinkedObject = -> Revolve
FEATURE [App::FeaturePython] GroundedJoint001  # Assembly grounded joint (typed FeaturePython)
  ObjectToGround = -> cylinterd
FEATURE [Assembly::JointGroup] Joints001
  Group = -> [GroundedJoint001]
FEATURE [App::Link] boss  label="boss001"
  LinkPlacement = pos=(-1.89289,-0.521303,-0.130738) rot=(0,0,1;0rad)
  LinkedObject = -> Extrude
  Placement = pos=(-1.89289,-0.521303,-0.130738) rot=(0,0,1;0rad)
FEATURE [Assembly::AssemblyObject] Assembly001  label="si"
  Group = -> [Joints001,cylinterd,GroundedJoint001,boss]
  Origin = -> Origin006
  Placement = pos=(0,0,0) rot=(0.987688,0,-0.156434;3.14159rad)
  Type = Assembly
FEATURE [App::Link] cylinterd001  label="cylinterd002"
  LinkedObject = -> cylinterd
FEATURE [App::Link] boss001  label="boss002"
  LinkPlacement = pos=(-1.89289,-0.521303,-0.130738) rot=(0,0,1;0rad)
  LinkedObject = -> boss
  Placement = pos=(-1.89289,-0.521303,-0.130738) rot=(0,0,1;0rad)
FEATURE [Assembly::AssemblyLink] si  label="si001"
  Group = -> [cylinterd001,boss001]
  LinkedObject = -> Assembly001
  Origin = -> Origin007
  Placement = pos=(0,20,-3) rot=(1,0,0;3.14159rad)
  Rigid = true
FEATURE [PartDesign::Pad] Pad010
  BaseFeature = -> Chamfer002
  Direction = (0,0,1)
  Length = 13
  Length2 = 10
  Profile = -> Sketch016
  ReferenceAxis = -> Sketch016 [N_Axis]
  Suppressed = false
  Type = 0
FEATURE [PartDesign::Body] Body003  label="tailhk"
  AllowCompound = false
  Group = -> [Sketch014,Pad009,Sketch015,Pocket001,Chamfer002,Sketch016,Pad010]
  Origin = -> Origin004
  Tip = -> Pad010
FEATURE [Sketcher::SketchObject] Sketch017  label="cope"
  ArcFitTolerance = 1e-06
  FullyConstrained = true
  MakeInternals = false
  Placement = pos=(0,0,0) rot=(1,0,0;1.5708rad)
  sketch-geometry (6):
    g0: LineSegment StartX=14 StartY=0 StartZ=0 EndX=6 EndY=3 EndZ=0
    g1: LineSegment StartX=6 StartY=3 StartZ=0 EndX=6 EndY=5 EndZ=0
    g2: LineSegment StartX=6 StartY=5 StartZ=0 EndX=0 EndY=5 EndZ=0
    g3: LineSegment StartX=14 StartY=0 StartZ=0 EndX=14 EndY=6 EndZ=0
    g4: LineSegment StartX=14 StartY=6 StartZ=0 EndX=0 EndY=6 EndZ=0
    g5: LineSegment StartX=0 StartY=6 StartZ=0 EndX=0 EndY=5 EndZ=0
  constraints (18):
    c: DistanceY(g0,g0) = 3
    c: Distance(g0,g-2) = 6
    c: Coincident(g0,g1)
    c: Vertical(g1)
    c: Coincident(g1,g2)
    c: PointOnObject(g2,g-2)
    c: Horizontal(g2)
    c: DistanceY(g1,g1) = 2
    c: PointOnObject(g0,g-1)
    c: DistanceX(g-1,g0) = 14
    c: Coincident(g0,g3)
    c: Vertical(g3)
    c: Coincident(g3,g4)
    c: PointOnObject(g4,g-2)
    c: Horizontal(g4)
    c: Coincident(g4,g5)
    c: Coincident(g5,g2)
    c: DistanceY(g3,g3) = 6
FEATURE [PartDesign::Revolution] Revolution
  Angle = 180
  Angle2 = 60
  Axis = (0,-2e-16,1)
  Base = (0,0,0)
  Placement = pos=(0,0,0) rot=(1,0,0;1.5708rad)
  Profile = -> Sketch017
  ReferenceAxis = -> Sketch017 [V_Axis]
  Reversed = true
  Suppressed = false
  Type = 0
FEATURE [Sketcher::SketchObject] Sketch018
  ArcFitTolerance = 1e-06
  AttachmentSupport = -> [Revolution]
  ExternalGeometry = -> [Revolution]
  FullyConstrained = true
  MakeInternals = false
  MapMode = 5
  Placement = pos=(0,0,6) rot=(0,0,1;3.14159rad)
  sketch-geometry (7):
    g0: LineSegment StartX=14 StartY=0 StartZ=0 EndX=14 EndY=29 EndZ=0
    g1: LineSegment StartX=14 StartY=29 StartZ=0 EndX=-14 EndY=29 EndZ=0
    g2: LineSegment StartX=-14 StartY=29 StartZ=0 EndX=-14 EndY=-3.6e-15 EndZ=0
    g3: GeomPoint X=0 Y=20 Z=0
    g4: GeomPoint X=0 Y=29 Z=0
    g5: GeomPoint X=0 Y=14 Z=0
    g6: ArcOfCircle CenterX=4.208e-13 CenterY=2.6e-15 CenterZ=0 NormalX=0 NormalY=0 NormalZ=1 AngleXU=0 Radius=14 StartAngle=0 EndAngle=3.14159
  constraints (15):
    c: Coincident(g0,g1)
    c: Coincident(g1,g2)
    c: Vertical(g0)
    c: Vertical(g2)
    c: Horizontal(g1)
    c: Coincident(g0,g-3)
    c: Coincident(g-4,g2)
    c: PointOnObject(g3,g-2)
    c: Symmetric(g1,g1,g4)
    c: DistanceY(g3,g4) = 9
    c: DistanceY(g-1,g3) = 20
    c: PointOnObject(g5,g-5)
    c: PointOnObject(g5,g-2)
    c: Perpendicular(g-3,g6) = 4.71239
    c: Coincident(g6,g2)
FEATURE [PartDesign::Pad] Pad011
  BaseFeature = -> Revolution
  Direction = (0,0,1)
  Length = 10
  Length2 = 10
  Placement = pos=(0,0,0) rot=(1,0,0;1.5708rad)
  Profile = -> Sketch018
  ReferenceAxis = -> Sketch018 [N_Axis]
  Reversed = true
  Suppressed = false
  Type = 0
FEATURE [Sketcher::SketchObject] Sketch019
  ArcFitTolerance = 1e-06
  AttachmentSupport = -> [Pad011]
  ExternalGeometry = -> [Pad011]
  FullyConstrained = true
  MakeInternals = false
  MapMode = 5
  Placement = pos=(0,0,6) rot=(0,0,1;3.14159rad)
  sketch-geometry (8):
    g0: GeomPoint X=0 Y=20 Z=0
    g1: LineSegment StartX=5.7735 StartY=20 StartZ=0 EndX=2.88675 EndY=25 EndZ=0
    g2: LineSegment StartX=2.88675 StartY=25 StartZ=0 EndX=-2.88675 EndY=25 EndZ=0
    g3: LineSegment StartX=-2.88675 StartY=25 StartZ=0 EndX=-5.7735 EndY=20 EndZ=0
    g4: LineSegment StartX=-5.7735 StartY=20 StartZ=0 EndX=-2.88675 EndY=15 EndZ=0
    g5: LineSegment StartX=-2.88675 StartY=15 StartZ=0 EndX=2.88675 EndY=15 EndZ=0
    g6: LineSegment StartX=2.88675 StartY=15 StartZ=0 EndX=5.7735 EndY=20 EndZ=0
    g7: Circle [constr] CenterX=0 CenterY=20 CenterZ=0 NormalX=0 NormalY=0 NormalZ=1 AngleXU=0 Radius=5.7735
  constraints (18):
    c: PointOnObject(g0,g-2)
    c: DistanceY(g-1,g0) = 20
    c: Coincident(g1,g2)
    c: Coincident(g2,g3)
    c: Coincident(g3,g4)
    c: Coincident(g4,g5)
    c: Coincident(g5,g6)
    c: Coincident(g6,g1)
    c: Equal(g1, g2-g6) x5
    c: PointOnObject(g1,g7)
    c: PointOnObject(g2,g7)
    c: PointOnObject(g3,g7)
    c: PointOnObject(g4,g7)
    c: PointOnObject(g5,g7)
    c: PointOnObject(g6,g7)
    c: Coincident(g7,g0)
    c: Horizontal(g2)
    c: Distance(g2,g1) = 10
FEATURE [PartDesign::Pocket] Pocket002
  BaseFeature = -> Pad011
  Direction = (0,0,-1)
  Length = 5
  Length2 = 5
  Placement = pos=(0,0,0) rot=(1,0,0;1.5708rad)
  Profile = -> Sketch019
  ReferenceAxis = -> Sketch019 [N_Axis]
  Suppressed = false
  Type = 0
FEATURE [Sketcher::SketchObject] Sketch020
  ArcFitTolerance = 1e-06
  AttachmentSupport = -> [Pocket002]
  FullyConstrained = true
  MakeInternals = false
  MapMode = 5
  Placement = pos=(0,0,1) rot=(0,0,1;3.14159rad)
  sketch-geometry (2):
    g0: GeomPoint X=0 Y=20 Z=0
    g1: Circle CenterX=0 CenterY=20 CenterZ=0 NormalX=0 NormalY=0 NormalZ=1 AngleXU=0 Radius=3
  constraints (4):
    c: PointOnObject(g0,g-2)
    c: DistanceY(g-1,g0) = 20
    c: Coincident(g1,g0)
    c: Diameter(g1) = 6
FEATURE [PartDesign::Pocket] Pocket003
  BaseFeature = -> Pocket002
  Direction = (0,0,-1)
  Length = 5
  Length2 = 5
  Placement = pos=(0,0,0) rot=(1,0,0;1.5708rad)
  Profile = -> Sketch020
  ReferenceAxis = -> Sketch020 [N_Axis]
  Suppressed = false
  Type = 0
FEATURE [PartDesign::Body] Body005  label="fing"
  AllowCompound = false
  Group = -> [Sketch017,Revolution,Sketch018,Pad011,Sketch019,Pocket002,Sketch020,Pocket003]
  Origin = -> Origin008
  Tip = -> Pocket003
FEATURE [App::Link] fing  label="fing001"
  LinkPlacement = pos=(0,20,-66.9542) rot=(0,1,0;3.14159rad)
  LinkedObject = -> Body005
  Placement = pos=(0,20,-66.9542) rot=(0,1,0;3.14159rad)
FEATURE [App::FeaturePython] Joint004  label="Slider"  # Assembly joint (typed FeaturePython)
  Activated = true
  AngleMax = 0
  AngleMin = 0
  Detach1 = false
  Detach2 = false
  Distance = 0
  Distance2 = 0
  EnableAngleMax = false
  EnableAngleMin = false
  EnableLengthMax = false
  EnableLengthMin = false
  JointType = 3 (Slider)
  LengthMax = 0
  LengthMin = 0
  Placement1 = pos=(0,0,-68.5) rot=(1,0,0;3.14159rad)
  Placement2 = pos=(0,-20,-1.5) rot=(0,0,1;3.14159rad)
  Reference1 = -> Assembly [m6.Face14,m6.Face14]
  Reference2 = -> Assembly [fing.Face13,fing.Face13]
FEATURE [App::FeaturePython] Joint005  label="Fixed001"  # Assembly joint (typed FeaturePython)
  Activated = true
  AngleMax = 0
  AngleMin = 0
  Detach1 = false
  Detach2 = false
  Distance = 0
  Distance2 = 0
  EnableAngleMax = false
  EnableAngleMin = false
  EnableLengthMax = false
  EnableLengthMin = false
  JointType = 0 (Fixed)
  LengthMax = 0
  LengthMin = 0
  Placement1 = pos=(-2.77128,-4.8,0) rot=(0,0,1;0rad)
  Placement2 = pos=(2.88675,-15,1) rot=(0,0,1;0rad)
  Reference1 = -> Assembly [m6b.Face8,m6b.Vertex9]
  Reference2 = -> Assembly [fing.Face20,fing.Vertex29]
FEATURE [Assembly::JointGroup] Joints
  Group = -> [GroundedJoint,Joint,Joint001,Joint002,Joint003,Joint004,Joint005]
FEATURE [Assembly::AssemblyObject] Assembly
  Group = -> [Joints,m6,GroundedJoint,m6b,Joint,Joint001,tailhk,Joint002,Joint003,Body004,si,fing,Joint004,Joint005]
  Origin = -> Origin003
  Type = Assembly
